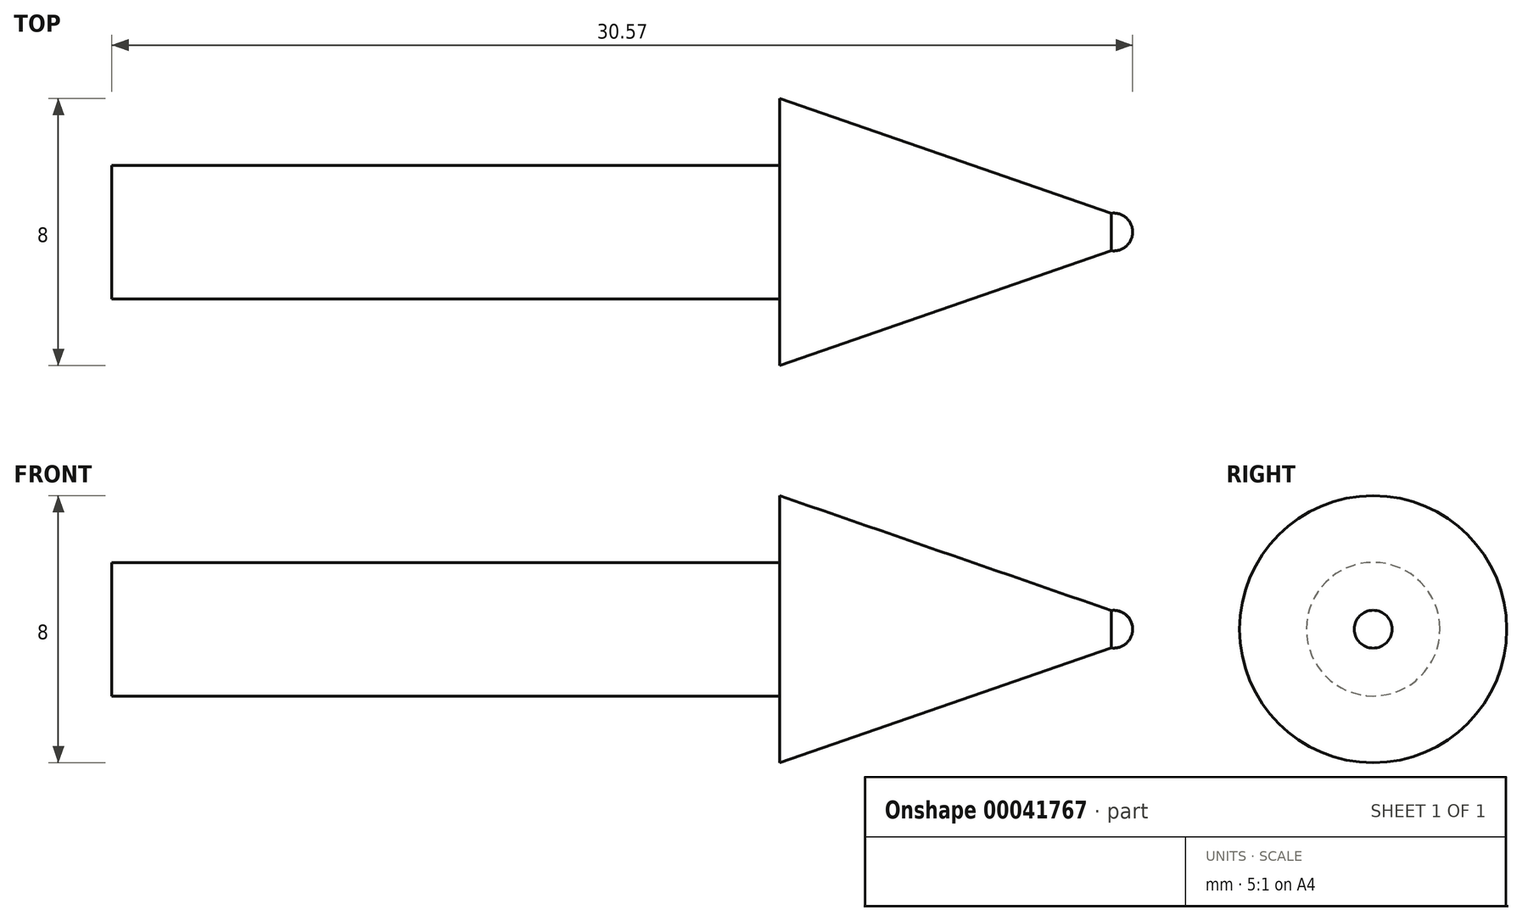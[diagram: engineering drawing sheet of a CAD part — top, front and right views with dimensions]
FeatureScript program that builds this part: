
annotation { "Feature Type Name" : "Feature", "Feature Type Description" : "" }
export const myFeature = defineFeature(function(context is Context, id is Id, definition is map)
    precondition{}
    {
        {
            var Q0;
            Q0=qCreatedBy(makeId("Front.planeOp"),FACE);
            var sketch = newSketch(context, id + "F0", { "sketchPlane" : qUnion([Q0])});
            skLineSegment(sketch, "E0", {"start": v(0, 0) * mm, "end": v(30, 0) * mm});
            skLineSegment(sketch, "E1", {"start": v(0, 0) * mm, "end": v(0, 2) * mm});
            skLineSegment(sketch, "E2", {"start": v(0, 2) * mm, "end": v(20, 2) * mm});
            skLineSegment(sketch, "E3", {"start": v(20, 2) * mm, "end": v(20, 4) * mm});
            skPoint(sketch, "E4.end.orphan", {"position": v(30, 1.07) * mm});
            skLineSegment(sketch, "E5", {"start": v(20, 4) * mm, "end": v(29.93, 0.56) * mm});
            skLineSegment(sketch, "E6", {"start": v(30, 0) * mm, "end": v(30.57, 0) * mm});
            skArc(sketch, "E7", {"start": v(30.57, 0) * mm, "mid": v(30.37, 0.43) * mm, "end": v(29.93, 0.56) * mm});
            skSolve(sketch);
        }
        {
            var Q0;
            Q0 = qSketchRegion(id + "F0", true);
            var Q1;
            Q1=sQuery(id+"F0.wireOp",EDGE,"E0");
            revolve(context, id + "F1", {"entities" : qUnion([Q0]), "axis" : qUnion([Q1]), "revolveType" : RevolveType.FULL});
        }
    });
